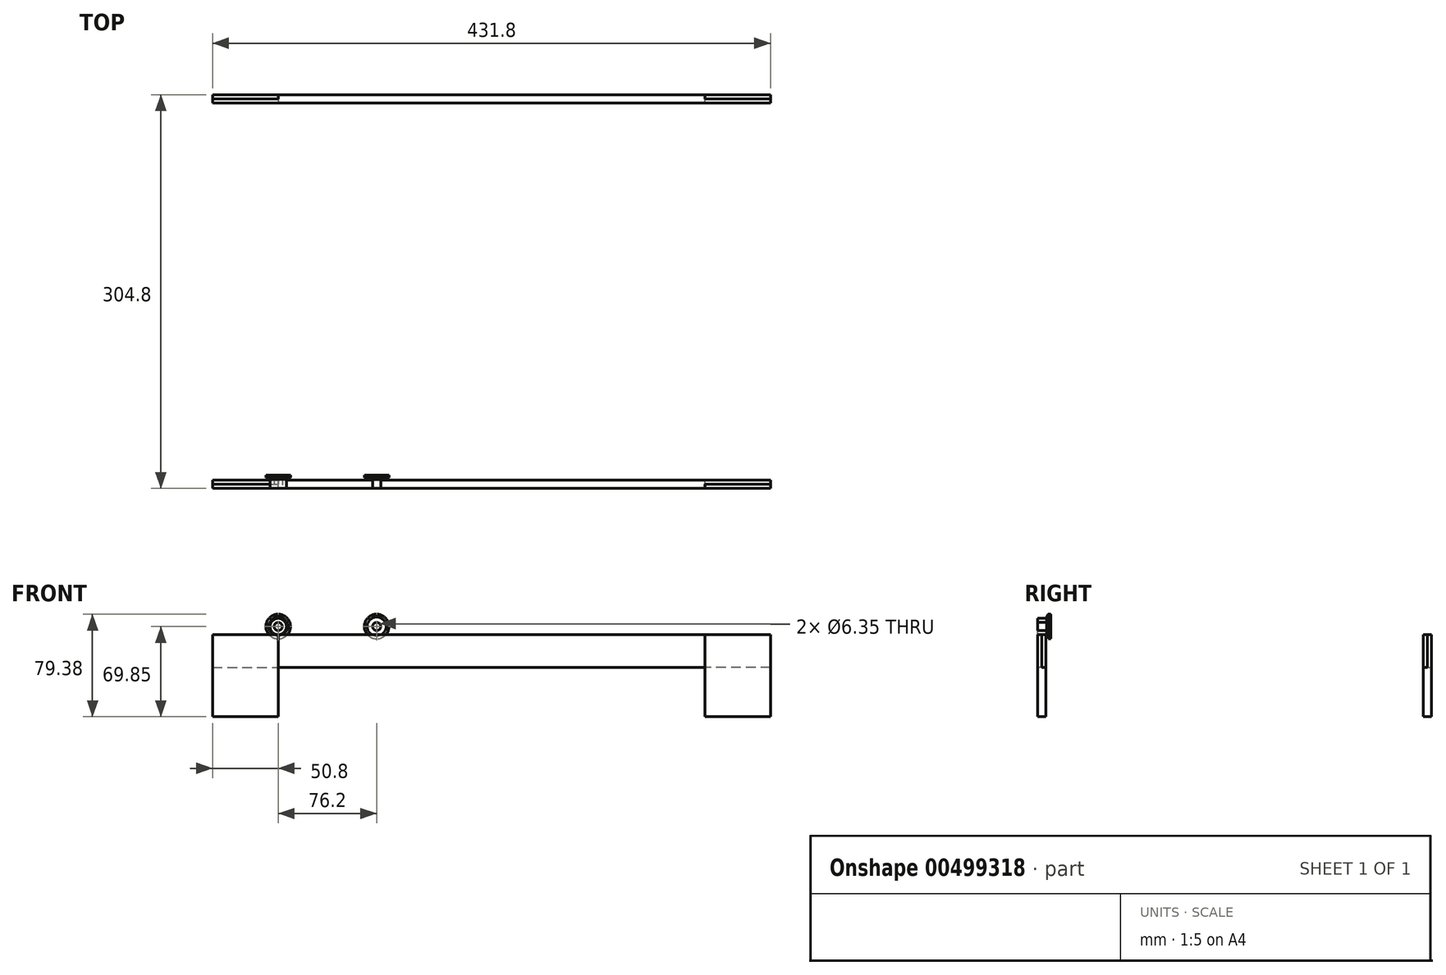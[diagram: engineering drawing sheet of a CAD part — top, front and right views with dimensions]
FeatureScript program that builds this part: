
annotation { "Feature Type Name" : "Feature", "Feature Type Description" : "" }
export const myFeature = defineFeature(function(context is Context, id is Id, definition is map)
    precondition{}
    {
        {
            var Q0;
            Q0=qCreatedBy(makeId("Top.planeOp"),FACE);
            var sketch = newSketch(context, id + "F0", { "sketchPlane" : qUnion([Q0])});
            skLineSegment(sketch, "E0.bottom", {"start": v(0, -190.5) * mm, "end": v(-508, -190.5) * mm});
            skLineSegment(sketch, "E0.top", {"start": v(0, 190.5) * mm, "end": v(-508, 190.5) * mm});
            skLineSegment(sketch, "E0.left", {"start": v(0, -190.5) * mm, "end": v(0, 190.5) * mm});
            skLineSegment(sketch, "E0.right", {"start": v(-508, -190.5) * mm, "end": v(-508, 190.5) * mm});
            skPoint(sketch, "E0.middle", {"position": v(-254, 0) * mm});
            skLineSegment(sketch, "E1.bottom", {"start": v(0, 152.4) * mm, "end": v(431.8, 152.4) * mm});
            skLineSegment(sketch, "E1.top", {"start": v(0, -152.4) * mm, "end": v(431.8, -152.4) * mm});
            skLineSegment(sketch, "E1.left", {"start": v(0, 152.4) * mm, "end": v(0, -152.4) * mm});
            skLineSegment(sketch, "E1.right", {"start": v(431.8, 152.4) * mm, "end": v(431.8, -152.4) * mm});
            skPoint(sketch, "E1.middle", {"position": v(215.9, 0) * mm});
            skSolve(sketch);
        }
        {
            var Q0;
            Q0=makeQuery(id+"F0.imprint","IMPRINT",FACE,{"disambiguationData":[TD([[makeQuery(id+"F0.imprint","IMPRINT",EDGE,{"derivedFrom":sQuery(id+"F0.wireOp",EDGE,"E1.bottom")}),-1.0]])]});
            var sketch = newSketch(context, id + "F1", { "sketchPlane" : qUnion([Q0])});
            skLineSegment(sketch, "E2.bottom", {"start": v(0, -152.4) * mm, "end": v(50.8, -152.4) * mm});
            skLineSegment(sketch, "E2.top", {"start": v(0, -146.05) * mm, "end": v(50.8, -146.05) * mm});
            skLineSegment(sketch, "E2.left", {"start": v(0, -152.4) * mm, "end": v(0, -146.05) * mm});
            skLineSegment(sketch, "E2.right", {"start": v(50.8, -152.4) * mm, "end": v(50.8, -146.05) * mm});
            skLineSegment(sketch, "E3.bottom", {"start": v(0, 152.4) * mm, "end": v(50.8, 152.4) * mm});
            skLineSegment(sketch, "E3.top", {"start": v(0, 146.05) * mm, "end": v(50.8, 146.05) * mm});
            skLineSegment(sketch, "E3.left", {"start": v(0, 152.4) * mm, "end": v(0, 146.05) * mm});
            skLineSegment(sketch, "E3.right", {"start": v(50.8, 152.4) * mm, "end": v(50.8, 146.05) * mm});
            skLineSegment(sketch, "E4.bottom", {"start": v(431.8, -152.4) * mm, "end": v(381, -152.4) * mm});
            skLineSegment(sketch, "E4.top", {"start": v(431.8, -146.05) * mm, "end": v(381, -146.05) * mm});
            skLineSegment(sketch, "E4.left", {"start": v(431.8, -152.4) * mm, "end": v(431.8, -146.05) * mm});
            skLineSegment(sketch, "E4.right", {"start": v(381, -152.4) * mm, "end": v(381, -146.05) * mm});
            skLineSegment(sketch, "E5.bottom", {"start": v(431.8, 152.4) * mm, "end": v(381, 152.4) * mm});
            skLineSegment(sketch, "E5.top", {"start": v(431.8, 146.05) * mm, "end": v(381, 146.05) * mm});
            skLineSegment(sketch, "E5.left", {"start": v(431.8, 152.4) * mm, "end": v(431.8, 146.05) * mm});
            skLineSegment(sketch, "E5.right", {"start": v(381, 152.4) * mm, "end": v(381, 146.05) * mm});
            skSolve(sketch);
        }
        {
            var Q0;
            Q0 = qSketchRegion(id + "F1", true);
            extrude(context, id + "F2", {"entities" : qUnion([Q0]), "depth" : 63.5 * mm, "offsetDistance" : 25.4 * mm});
        }
        {
            var Q0;
            Q0=makeQuery(id+"F2.opExtrude","CAP_FACE",FACE,{"disambiguationData":[OSD([sQuery(id+"F1.wireOp",EDGE,"E4.bottom"),sQuery(id+"F1.wireOp",EDGE,"E4.top"),sQuery(id+"F1.wireOp",EDGE,"E4.left"),sQuery(id+"F1.wireOp",EDGE,"E4.right")])],"isStart":false});
            var sketch = newSketch(context, id + "F3", { "sketchPlane" : qUnion([Q0])});
            skLineSegment(sketch, "E6.bottom", {"start": v(431.8, -146.05) * mm, "end": v(381, -146.05) * mm});
            skLineSegment(sketch, "E6.top", {"start": v(431.8, -149.23) * mm, "end": v(381, -149.23) * mm});
            skLineSegment(sketch, "E6.left", {"start": v(431.8, -146.05) * mm, "end": v(431.8, -149.23) * mm});
            skLineSegment(sketch, "E6.right", {"start": v(381, -146.05) * mm, "end": v(381, -149.23) * mm});
            skLineSegment(sketch, "E7.bottom", {"start": v(431.8, 146.05) * mm, "end": v(381, 146.05) * mm});
            skLineSegment(sketch, "E7.top", {"start": v(431.8, 149.22) * mm, "end": v(381, 149.22) * mm});
            skLineSegment(sketch, "E7.left", {"start": v(431.8, 146.05) * mm, "end": v(431.8, 149.22) * mm});
            skLineSegment(sketch, "E7.right", {"start": v(381, 146.05) * mm, "end": v(381, 149.22) * mm});
            skLineSegment(sketch, "E8.bottom", {"start": v(0, -146.05) * mm, "end": v(50.8, -146.05) * mm});
            skLineSegment(sketch, "E8.top", {"start": v(0, -149.22) * mm, "end": v(50.8, -149.22) * mm});
            skLineSegment(sketch, "E8.left", {"start": v(0, -146.05) * mm, "end": v(0, -149.22) * mm});
            skLineSegment(sketch, "E8.right", {"start": v(50.8, -146.05) * mm, "end": v(50.8, -149.22) * mm});
            skLineSegment(sketch, "E9.bottom", {"start": v(0, 149.23) * mm, "end": v(50.8, 149.23) * mm});
            skLineSegment(sketch, "E9.top", {"start": v(0, 146.05) * mm, "end": v(50.8, 146.05) * mm});
            skLineSegment(sketch, "E9.left", {"start": v(0, 149.23) * mm, "end": v(0, 146.05) * mm});
            skLineSegment(sketch, "E9.right", {"start": v(50.8, 149.23) * mm, "end": v(50.8, 146.05) * mm});
            skSolve(sketch);
        }
        {
            var Q0;
            Q0 = qSketchRegion(id + "F3", true);
            extrude(context, id + "F4", {"entities" : qUnion([Q0]), "operationType" : NewBodyOperationType.REMOVE, "oppositeDirection" : true, "depth" : 25.4 * mm, "offsetDistance" : 25.4 * mm});
        }
        {
            var Q0;
            Q0=makeQuery(id+"F2.opExtrude","SWEPT_FACE",FACE,{"disambiguationData":[OSD([sQuery(id+"F1.wireOp",EDGE,"E4.left")])]});
            var sketch = newSketch(context, id + "F5", { "sketchPlane" : qUnion([Q0])});
            skLineSegment(sketch, "E10.bottom", {"start": v(-146.05, 63.5) * mm, "end": v(-152.4, 63.5) * mm});
            skLineSegment(sketch, "E10.top", {"start": v(-146.05, 38.1) * mm, "end": v(-152.4, 38.1) * mm});
            skLineSegment(sketch, "E10.left", {"start": v(-146.05, 63.5) * mm, "end": v(-146.05, 38.1) * mm});
            skLineSegment(sketch, "E10.right", {"start": v(-152.4, 63.5) * mm, "end": v(-152.4, 38.1) * mm});
            skLineSegment(sketch, "E11.bottom", {"start": v(152.4, 63.5) * mm, "end": v(146.05, 63.5) * mm});
            skLineSegment(sketch, "E11.top", {"start": v(152.4, 38.1) * mm, "end": v(146.05, 38.1) * mm});
            skLineSegment(sketch, "E11.left", {"start": v(152.4, 63.5) * mm, "end": v(152.4, 38.1) * mm});
            skLineSegment(sketch, "E11.right", {"start": v(146.05, 63.5) * mm, "end": v(146.05, 38.1) * mm});
            skSolve(sketch);
        }
        {
            var Q0;
            Q0 = qSketchRegion(id + "F5", true);
            var Q1;
            Q1=makeQuery(id+"F2.opExtrude","SWEPT_FACE",FACE,{"disambiguationData":[OSD([sQuery(id+"F1.wireOp",EDGE,"E2.left")])]});
            extrude(context, id + "F6", {"entities" : qUnion([Q0]), "endBound" : BoundingType.UP_TO_SURFACE, "oppositeDirection" : true, "depth" : 25.4 * mm, "endBoundEntityFace" : qUnion([Q1]), "offsetDistance" : 25.4 * mm});
        }
        {
            var Q0;
            Q0=makeQuery(id+"F2.opExtrude","SWEPT_BODY",BODY,{"disambiguationData":[OSD([sQuery(id+"F1.wireOp",EDGE,"E5.bottom"),sQuery(id+"F1.wireOp",EDGE,"E5.top"),sQuery(id+"F1.wireOp",EDGE,"E5.left"),sQuery(id+"F1.wireOp",EDGE,"E5.right")])]});
            var Q1;
            Q1=makeQuery(id+"F2.opExtrude","SWEPT_BODY",BODY,{"disambiguationData":[OSD([sQuery(id+"F1.wireOp",EDGE,"E2.bottom"),sQuery(id+"F1.wireOp",EDGE,"E2.top"),sQuery(id+"F1.wireOp",EDGE,"E2.left"),sQuery(id+"F1.wireOp",EDGE,"E2.right")])]});
            var Q2;
            Q2=makeQuery(id+"F2.opExtrude","SWEPT_BODY",BODY,{"disambiguationData":[OSD([sQuery(id+"F1.wireOp",EDGE,"E4.bottom"),sQuery(id+"F1.wireOp",EDGE,"E4.top"),sQuery(id+"F1.wireOp",EDGE,"E4.left"),sQuery(id+"F1.wireOp",EDGE,"E4.right")])]});
            var Q3;
            Q3=makeQuery(id+"F2.opExtrude","SWEPT_BODY",BODY,{"disambiguationData":[OSD([sQuery(id+"F1.wireOp",EDGE,"E3.bottom"),sQuery(id+"F1.wireOp",EDGE,"E3.top"),sQuery(id+"F1.wireOp",EDGE,"E3.left"),sQuery(id+"F1.wireOp",EDGE,"E3.right")])]});
            var Q4;
            Q4=makeQuery(id+"F6.opExtrude","SWEPT_BODY",BODY,{"disambiguationData":[OSD([sQuery(id+"F5.wireOp",EDGE,"E11.bottom"),sQuery(id+"F5.wireOp",EDGE,"E11.top"),sQuery(id+"F5.wireOp",EDGE,"E11.left"),sQuery(id+"F5.wireOp",EDGE,"E11.right")])]});
            var Q5;
            Q5=makeQuery(id+"F6.opExtrude","SWEPT_BODY",BODY,{"disambiguationData":[OSD([sQuery(id+"F5.wireOp",EDGE,"E10.bottom"),sQuery(id+"F5.wireOp",EDGE,"E10.top"),sQuery(id+"F5.wireOp",EDGE,"E10.left"),sQuery(id+"F5.wireOp",EDGE,"E10.right")])]});
            booleanBodies(context, id + "F7", {"operationType" : BooleanOperationType.SUBTRACTION, "tools" : qUnion([Q0, Q1, Q2, Q3]), "targets" : qUnion([Q4, Q5]), "keepTools" : true});
        }
        {
            var Q0;
            Q0=makeQuery(id+"F6.opExtrude","SWEPT_FACE",FACE,{"disambiguationData":[OSD([sQuery(id+"F5.wireOp",EDGE,"E10.right")])]});
            var sketch = newSketch(context, id + "F8", { "sketchPlane" : qUnion([Q0])});
            skCircle(sketch, "E12", {"center": v(50.8, 69.85) * mm, "radius": 6.35 * mm});
            skCircle(sketch, "E13", {"center": v(50.8, 69.85) * mm, "radius": 9.53 * mm});
            skCircle(sketch, "E14", {"center": v(50.8, 69.85) * mm, "radius": 3.18 * mm});
            skLineSegment(sketch, "E15", {"start": v(88.9, 95.03) * mm, "end": v(88.9, 74.29) * mm});
            skCircle(sketch, "E16.MirrorC", {"center": v(127, 69.85) * mm, "radius": 9.53 * mm});
            skCircle(sketch, "E17.MirrorC", {"center": v(127, 69.85) * mm, "radius": 6.35 * mm});
            skCircle(sketch, "E18.MirrorC", {"center": v(127, 69.85) * mm, "radius": 3.18 * mm});
            skSolve(sketch);
        }
        {
            var Q0;
            Q0=makeQuery(id+"F8.imprint","IMPRINT",FACE,{"disambiguationData":[TD([[makeQuery(id+"F8.imprint","IMPRINT",EDGE,{"derivedFrom":sQuery(id+"F8.wireOp",EDGE,"E12")}),1.0]])]});
            var Q1;
            Q1=makeQuery(id+"F8.imprint","IMPRINT",FACE,{"disambiguationData":[TD([[makeQuery(id+"F8.imprint","IMPRINT",EDGE,{"derivedFrom":sQuery(id+"F8.wireOp",EDGE,"E18.MirrorC")}),1.0]])]});
            var Q2;
            Q2=makeQuery(id+"F6.opExtrude","SWEPT_FACE",FACE,{"disambiguationData":[OSD([sQuery(id+"F5.wireOp",EDGE,"E10.left")])]});
            extrude(context, id + "F9", {"entities" : qUnion([Q0, Q1]), "endBound" : BoundingType.UP_TO_SURFACE, "oppositeDirection" : true, "depth" : 25.4 * mm, "endBoundEntityFace" : qUnion([Q2]), "hasOffset" : true, "offsetDistance" : -0.5 * mm});
        }
        {
            var Q0;
            Q0=makeQuery(id+"F9.opExtrude","CAP_FACE",FACE,{"disambiguationData":[OSD([sQuery(id+"F8.wireOp",EDGE,"E12"),sQuery(id+"F8.wireOp",EDGE,"E14")])],"isStart":false});
            var sketch = newSketch(context, id + "F10", { "sketchPlane" : qUnion([Q0])});
            skCircle(sketch, "E19.0", {"center": v(-50.8, 69.85) * mm, "radius": 3.17 * mm});
            skCircle(sketch, "E20", {"center": v(-50.8, 69.85) * mm, "radius": 9.53 * mm});
            skCircle(sketch, "E21.0", {"center": v(-127, 69.85) * mm, "radius": 3.18 * mm});
            skCircle(sketch, "E22", {"center": v(-127, 69.85) * mm, "radius": 9.53 * mm});
            skSolve(sketch);
        }
        {
            var Q0;
            Q0=makeQuery(id+"F10.imprint","IMPRINT",FACE,{"disambiguationData":[TD([[makeQuery(id+"F10.imprint","IMPRINT",EDGE,{"derivedFrom":sQuery(id+"F10.wireOp",EDGE,"E21.0")}),-1.0]])]});
            var Q1;
            Q1=makeQuery(id+"F10.imprint","IMPRINT",FACE,{"disambiguationData":[TD([[makeQuery(id+"F10.imprint","IMPRINT",EDGE,{"derivedFrom":sQuery(id+"F10.wireOp",EDGE,"E19.0")}),-1.0]])]});
            var Q2;
            Q2=makeQuery(id+"F10.imprint","IMPRINT",FACE,{"disambiguationData":[TD([[makeQuery(id+"F10.imprint","IMPRINT",EDGE,{"derivedFrom":sQuery(id+"F10.wireOp",EDGE,"E20")}),1.0]])]});
            extrude(context, id + "F11", {"entities" : qUnion([Q0, Q1, Q2]), "operationType" : NewBodyOperationType.ADD, "depth" : 3.17 * mm, "offsetDistance" : 25.4 * mm});
        }
        {
            var Q0;
            Q0=makeQuery(id+"F11.opExtrude","CAP_EDGE",EDGE,{"disambiguationData":[OSD([sQuery(id+"F10.wireOp",EDGE,"E20")])],"isStart":true});
            var Q1;
            Q1=makeQuery(id+"F11.opExtrude","CAP_EDGE",EDGE,{"disambiguationData":[OSD([sQuery(id+"F10.wireOp",EDGE,"E22")])],"isStart":true});
            chamfer(context, id + "F12", {"entities" : qUnion([Q0, Q1]), "chamferType" : ChamferType.OFFSET_ANGLE, "width" : 1.27 * mm, "oppositeDirection" : false, "angle" : 60 * degree, "tangentPropagation" : true});
        }
    });
